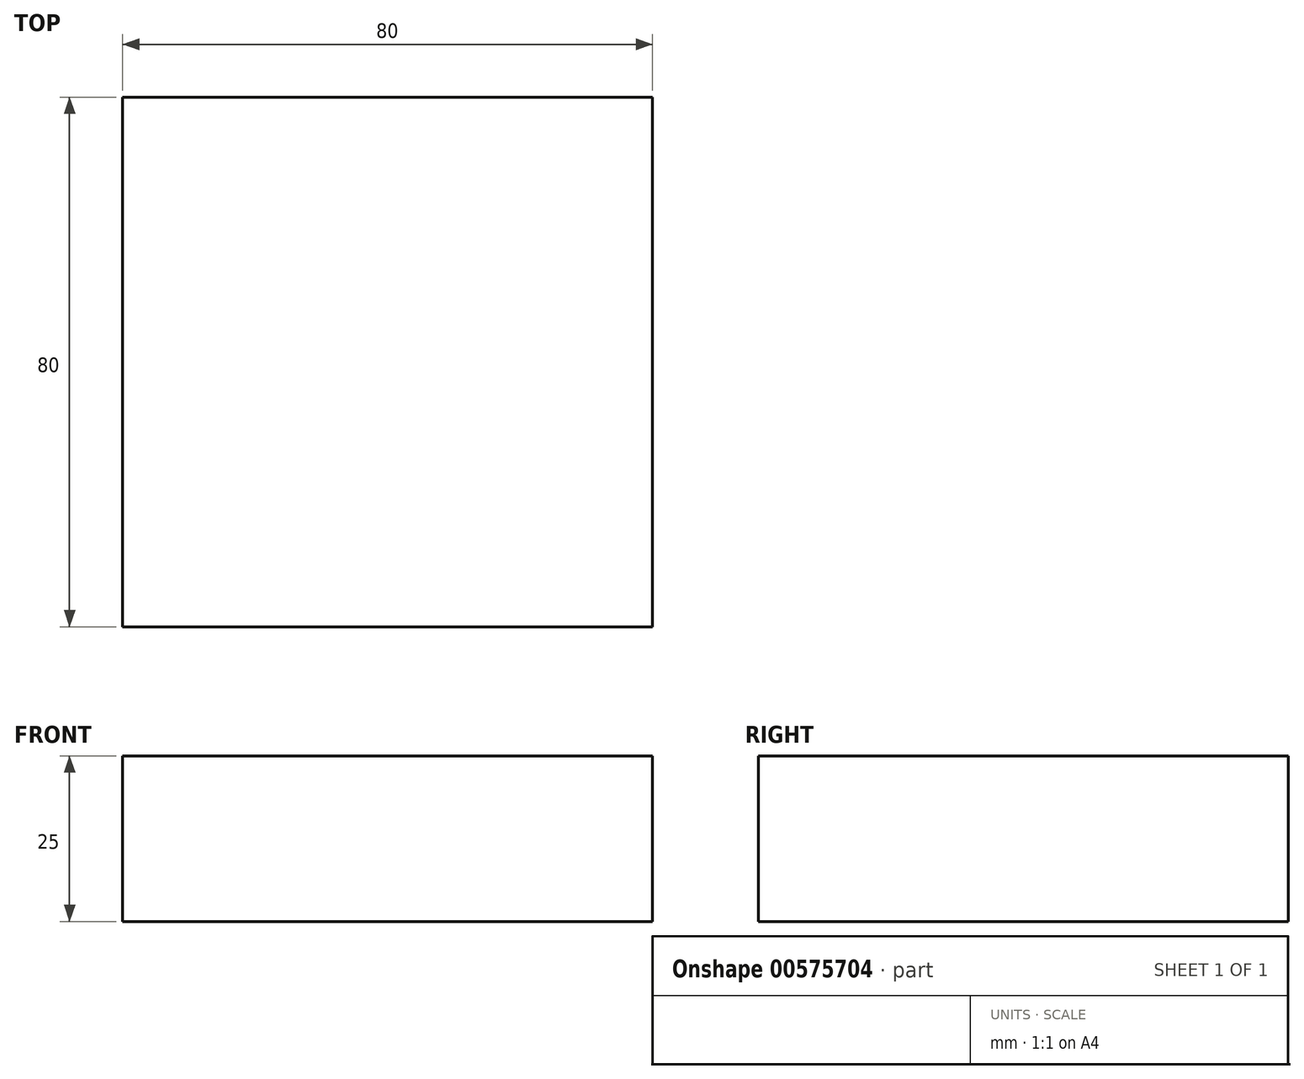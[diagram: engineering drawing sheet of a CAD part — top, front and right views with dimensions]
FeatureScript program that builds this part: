
annotation { "Feature Type Name" : "Feature", "Feature Type Description" : "" }
export const myFeature = defineFeature(function(context is Context, id is Id, definition is map)
    precondition{}
    {
        {
            var Q0;
            Q0=qCreatedBy(makeId("Top.planeOp"),FACE);
            var sketch = newSketch(context, id + "F0", { "sketchPlane" : qUnion([Q0])});
            skLineSegment(sketch, "E0.bottom", {"start": v(-40, 40) * mm, "end": v(40, 40) * mm});
            skLineSegment(sketch, "E0.top", {"start": v(-40, -40) * mm, "end": v(40, -40) * mm});
            skLineSegment(sketch, "E0.left", {"start": v(-40, 40) * mm, "end": v(-40, -40) * mm});
            skLineSegment(sketch, "E0.right", {"start": v(40, 40) * mm, "end": v(40, -40) * mm});
            skPoint(sketch, "E0.middle", {"position": v(0, 0) * mm});
            skSolve(sketch);
        }
        {
            var Q0;
            Q0 = qSketchRegion(id + "F0", true);
            extrude(context, id + "F1", {"entities" : qUnion([Q0]), "depth" : 25 * mm, "offsetDistance" : 25 * mm});
        }
    });
